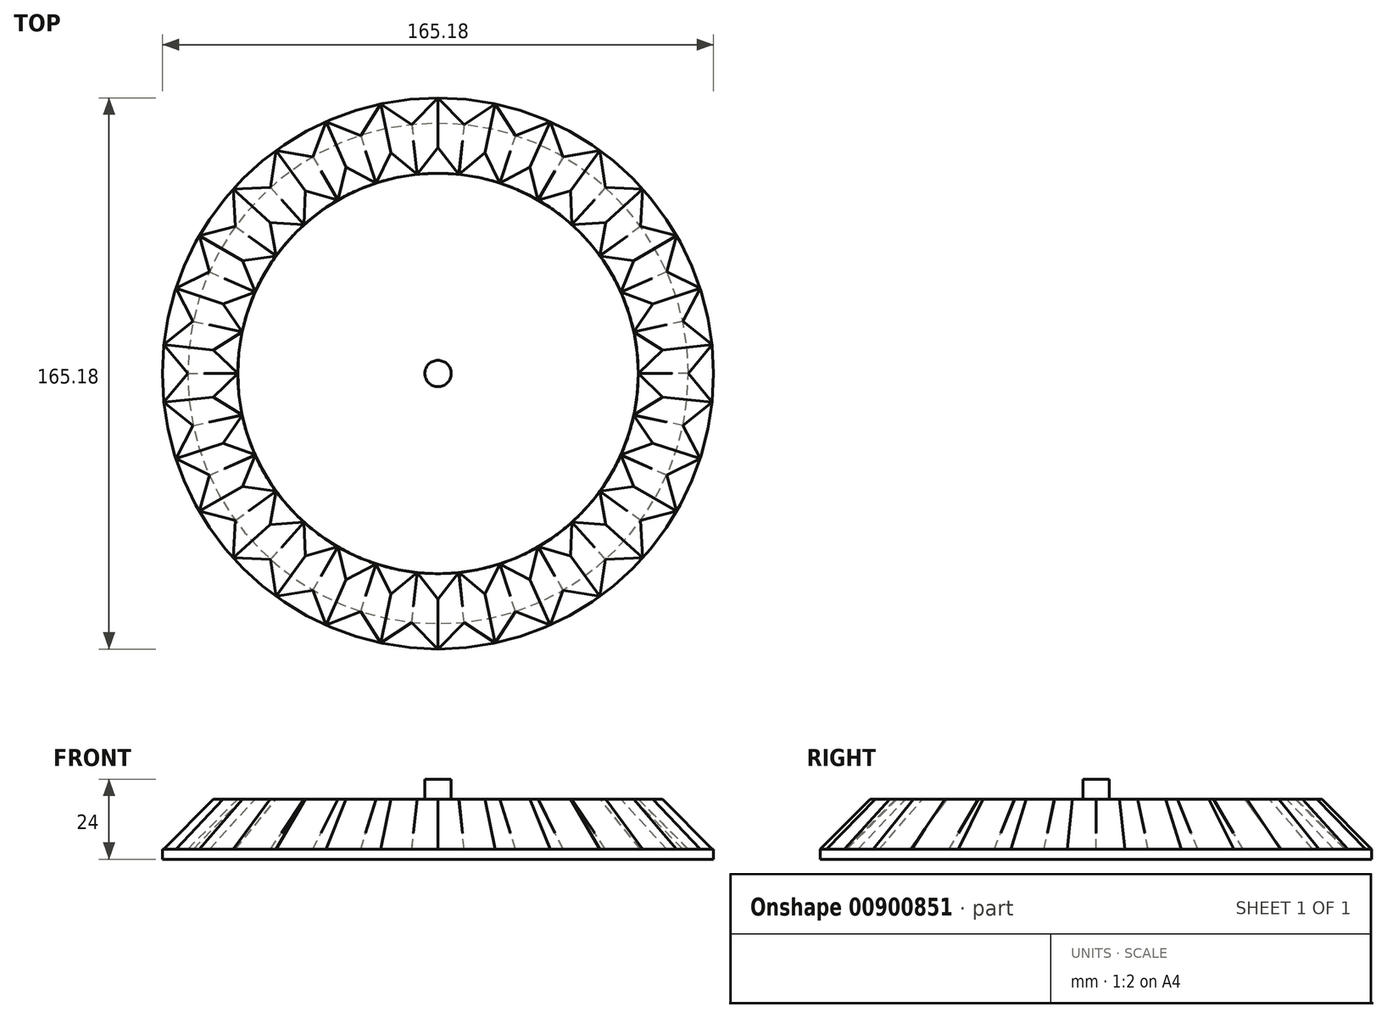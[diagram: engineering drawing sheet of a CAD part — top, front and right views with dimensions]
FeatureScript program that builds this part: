
annotation { "Feature Type Name" : "Feature", "Feature Type Description" : "" }
export const myFeature = defineFeature(function(context is Context, id is Id, definition is map)
    precondition{}
    {
        {
            var Q0;
            Q0=qCreatedBy(makeId("Top.planeOp"),FACE);
            var sketch = newSketch(context, id + "F0", { "sketchPlane" : qUnion([Q0])});
            skCircle(sketch, "E0", {"center": v(0, 0) * mm, "radius": 75 * mm});
            skSolve(sketch);
        }
        {
            var Q0;
            Q0=qSketchRegion(id+"F0",true);
            extrude(context, id + "F1", {"entities" : qUnion([Q0]), "depth" : 15 * mm, "offsetDistance" : 25 * mm, "hasDraft" : true, "draftAngle" : 45 * degree, "draftPullDirection" : true});
        }
        {
            var Q0;
            Q0=qCreatedBy(makeId("Top.planeOp"),FACE);
            var sketch = newSketch(context, id + "F2", { "sketchPlane" : qUnion([Q0])});
            skLineSegment(sketch, "E1", {"start": v(0, 82.59) * mm, "end": v(-7.85, 74.59) * mm});
            skLineSegment(sketch, "E2", {"start": v(-7.85, 74.59) * mm, "end": v(7.85, 74.59) * mm});
            skLineSegment(sketch, "E3", {"start": v(7.85, 74.59) * mm, "end": v(0, 82.59) * mm});
            skSolve(sketch);
        }
        {
            var Q0;
            Q0=makeQuery(id+"F1.opExtrude","CAP_FACE",FACE,{"disambiguationData":[OSD([sQuery(id+"F0.wireOp",EDGE,"E0")])],"isStart":false});
            var sketch = newSketch(context, id + "F3", { "sketchPlane" : qUnion([Q0])});
            skLineSegment(sketch, "E4", {"start": v(0, 67.67) * mm, "end": v(-6.25, 59.67) * mm});
            skLineSegment(sketch, "E5", {"start": v(-6.25, 59.67) * mm, "end": v(6.25, 59.67) * mm});
            skLineSegment(sketch, "E6", {"start": v(6.25, 59.67) * mm, "end": v(0, 67.67) * mm});
            skSolve(sketch);
        }
        {
            var Q1;
            Q1=makeQuery(id+"F2.imprint","IMPRINT",FACE,{"disambiguationData":[TD([[makeQuery(id+"F2.imprint","IMPRINT",EDGE,{"derivedFrom":sQuery(id+"F2.wireOp",EDGE,"E1")}),1.0]])]});
            var Q2;
            {var subQ0=sQuery(id+"F3.wireOp",EDGE,"E4");Q2=makeQuery(id+"F3.imprint","IMPRINT",FACE,{"disambiguationData":[TD([[makeQuery(id+"F3.imprint","IMPRINT",EDGE,{"derivedFrom":subQ0}),1.0]])]});}
            loft(context, id + "F4", {"sheetProfilesArray" : [{ "sheetProfileEntities" : qUnion([Q1]) }, { "sheetProfileEntities" : qUnion([Q2]) }]});
        }
        {
            var Q0;
            Q0=qCreatedBy(makeId("Front.planeOp"),FACE);
            var sketch = newSketch(context, id + "F5", { "sketchPlane" : qUnion([Q0])});
            skLineSegment(sketch, "E7", {"start": v(0, 30.95) * mm, "end": v(0, 0) * mm, "construction": true});
            skSolve(sketch);
        }
        {
            var Q0;
            {var subQ0=sQuery(id+"F3.wireOp",EDGE,"E4");Q0=makeQuery(id+"F4.opLoft","SWEPT_BODY",BODY,{"disambiguationData":[OSD([makeQuery(id+"F2.imprint","IMPRINT",FACE,{"disambiguationData":[TD([[makeQuery(id+"F2.imprint","IMPRINT",EDGE,{"derivedFrom":sQuery(id+"F2.wireOp",EDGE,"E1")}),1.0]])]}),makeQuery(id+"F3.imprint","IMPRINT",FACE,{"disambiguationData":[TD([[makeQuery(id+"F3.imprint","IMPRINT",EDGE,{"derivedFrom":subQ0}),1.0]])]})])]});}
            var Q1;
            Q1=sQuery(id+"F5.wireOp",EDGE,"E7");
            circularPattern(context, id + "F6", {"entities" : qUnion([Q0]), "axis" : qUnion([Q1]), "angle" : 360 * degree, "instanceCount" : 30, "equalSpace" : true});
        }
        {
            var Q0;
            Q0=makeQuery(id+"F1.opExtrude","CAP_FACE",FACE,{"disambiguationData":[OSD([sQuery(id+"F0.wireOp",EDGE,"E0")])],"isStart":true});
            var sketch = newSketch(context, id + "F7", { "sketchPlane" : qUnion([Q0])});
            skCircle(sketch, "E8", {"center": v(0, 0) * mm, "radius": 82.59 * mm});
            skSolve(sketch);
        }
        {
            var Q0;
            Q0=qSketchRegion(id+"F7",true);
            extrude(context, id + "F8", {"entities" : qUnion([Q0]), "depth" : 3 * mm, "offsetDistance" : 25 * mm});
        }
        {
            var Q0;
            Q0=makeQuery(id+"F1.opExtrude","CAP_FACE",FACE,{"disambiguationData":[OSD([sQuery(id+"F0.wireOp",EDGE,"E0")])],"isStart":false});
            var sketch = newSketch(context, id + "F9", { "sketchPlane" : qUnion([Q0])});
            skCircle(sketch, "E9", {"center": v(0, 0) * mm, "radius": 3.95 * mm});
            skSolve(sketch);
        }
        {
            var Q0;
            Q0=makeQuery(id+"F9.imprint","IMPRINT",FACE,{"disambiguationData":[TD([[makeQuery(id+"F9.imprint","IMPRINT",EDGE,{"derivedFrom":sQuery(id+"F9.wireOp",EDGE,"E9")}),1.0]])]});
            extrude(context, id + "F10", {"entities" : qUnion([Q0]), "operationType" : NewBodyOperationType.ADD, "depth" : 6 * mm, "offsetDistance" : 25 * mm});
        }
    });
